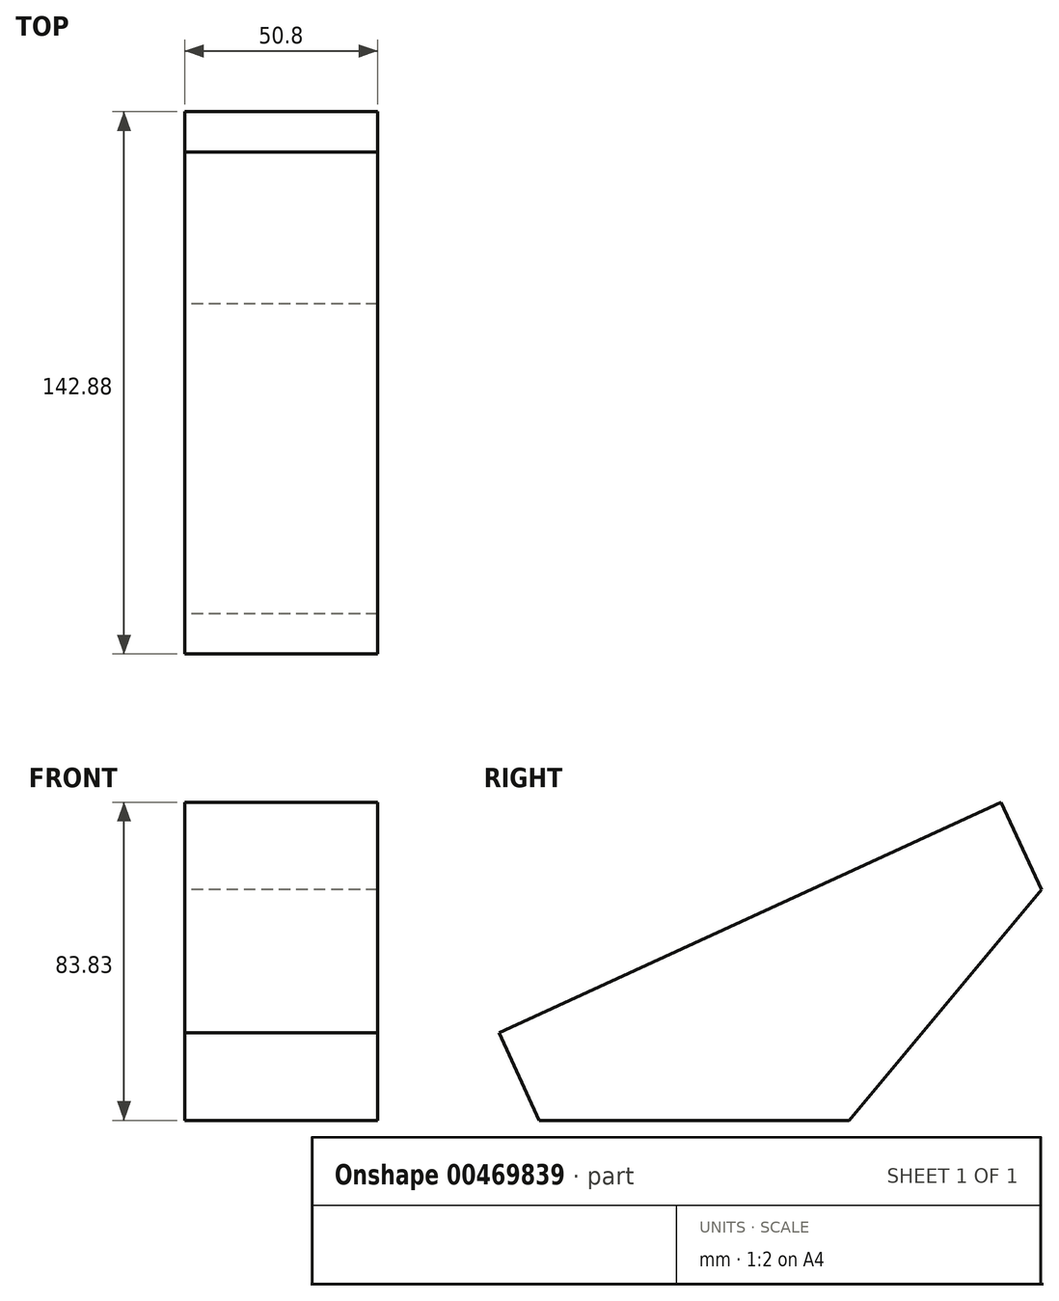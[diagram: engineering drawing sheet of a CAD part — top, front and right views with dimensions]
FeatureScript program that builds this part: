
annotation { "Feature Type Name" : "Feature", "Feature Type Description" : "" }
export const myFeature = defineFeature(function(context is Context, id is Id, definition is map)
    precondition{}
    {
        {
            var Q0;
            Q0=qCreatedBy(makeId("Right.planeOp"),FACE);
            var sketch = newSketch(context, id + "F0", { "sketchPlane" : qUnion([Q0])});
            skLineSegment(sketch, "E0", {"start": v(61.97, -12.83) * mm, "end": v(81.62, -12.83) * mm});
            skLineSegment(sketch, "E1", {"start": v(81.62, -12.83) * mm, "end": v(0, -12.83) * mm});
            skLineSegment(sketch, "E2", {"start": v(0, -12.83) * mm, "end": v(132.28, 47.92) * mm});
            skLineSegment(sketch, "E3", {"start": v(132.28, 47.92) * mm, "end": v(81.62, -12.83) * mm});
            skSolve(sketch);
        }
        {
            var Q0;
            {var subQ2=sQuery(id+"F0.wireOp",EDGE,"E2");Q0=makeQuery(id+"F0.imprint","IMPRINT",FACE,{"disambiguationData":[TD([[makeQuery(id+"F0.imprint","IMPRINT",EDGE,{"derivedFrom":subQ2}),-1.0]])]});}
            extrude(context, id + "F1", {"entities" : qUnion([Q0]), "depth" : 25.4 * mm});
        }
        {
            var Q0;
            Q0=makeQuery(id+"F1.opExtrude","CAP_FACE",FACE,{"disambiguationData":[OSD([sQuery(id+"F0.wireOp",EDGE,"E1"),sQuery(id+"F0.wireOp",EDGE,"E2"),sQuery(id+"F0.wireOp",EDGE,"E3")])],"isStart":false});
            extrude(context, id + "F2", {"entities" : qUnion([Q0]), "operationType" : NewBodyOperationType.ADD, "depth" : 25.4 * mm});
        }
        {
            var Q0;
            {var subQ0=sQuery(id+"F0.wireOp",EDGE,"E2");Q0=makeQuery(id+"F2.boolean.opBoolean","MERGE",FACE,{"derivedFrom":[makeQuery(id+"F1.opExtrude","SWEPT_FACE",FACE,{"disambiguationData":[OSD([subQ0])]}),makeQuery(id+"F2.opExtrude","SWEPT_FACE",FACE,{"disambiguationData":[OSD([subQ0])]})]});}
            extrude(context, id + "F3", {"entities" : qUnion([Q0]), "operationType" : NewBodyOperationType.ADD, "depth" : 25.4 * mm});
        }
    });
